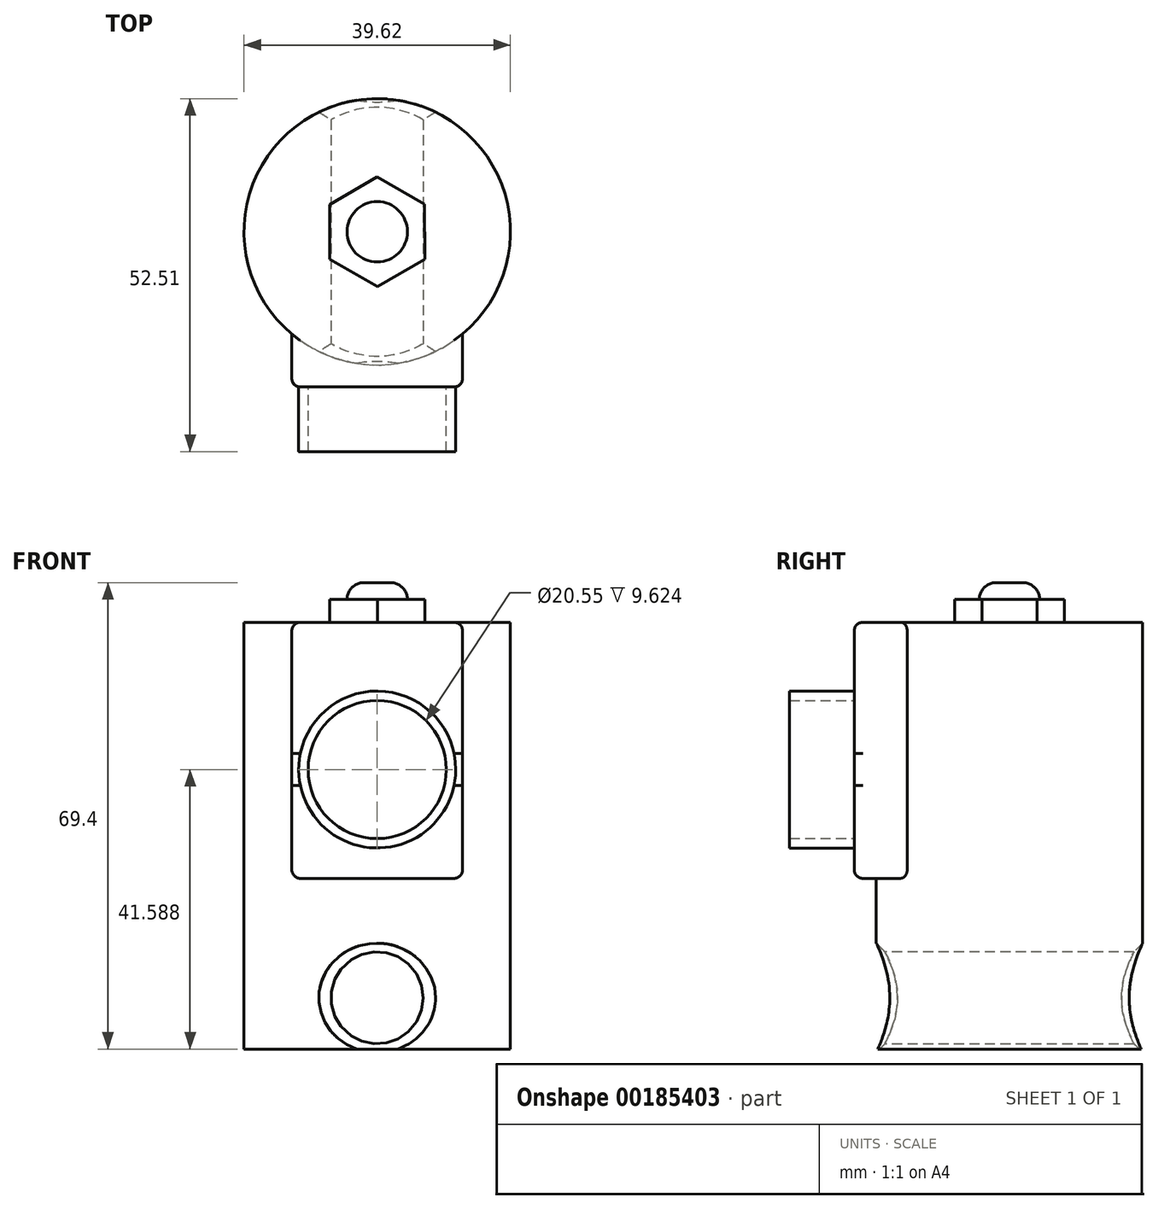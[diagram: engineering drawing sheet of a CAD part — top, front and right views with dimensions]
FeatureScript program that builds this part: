
annotation { "Feature Type Name" : "Feature", "Feature Type Description" : "" }
export const myFeature = defineFeature(function(context is Context, id is Id, definition is map)
    precondition{}
    {
        {
            var Q0;
            Q0=qCreatedBy(makeId("Top.planeOp"),FACE);
            var sketch = newSketch(context, id + "F0", { "sketchPlane" : qUnion([Q0])});
            skCircle(sketch, "E0", {"center": v(0, 0) * mm, "radius": 19.81 * mm});
            skLineSegment(sketch, "E1", {"start": v(0, 0) * mm, "end": v(0, -19.81) * mm});
            skSolve(sketch);
        }
        {
            var Q0;
            Q0 = qSketchRegion(id + "F0", true);
            extrude(context, id + "F1", {"entities" : qUnion([Q0]), "depth" : 63.5 * mm});
        }
        {
            var Q0;
            Q0=qCreatedBy(makeId("Right.planeOp"),FACE);
            var sketch = newSketch(context, id + "F2", { "sketchPlane" : qUnion([Q0])});
            skLineSegment(sketch, "E2", {"start": v(-19.81, 0) * mm, "end": v(-19.81, 70.78) * mm});
            skSolve(sketch);
        }
        {
            var Q0;
            Q0=sQuery(id+"F2.wireOp",EDGE,"E2");
            cPlane(context, id + "F3", {"entities" : qUnion([Q0]), "cplaneType" : CPlaneType.LINE_ANGLE, "offset" : 25.4 * mm, "angle" : 90 * degree, "width" : 152.4 * mm, "height" : 152.4 * mm});
        }
        {
            var Q0;
            Q0=qCreatedBy(id+"F3.planeOp",FACE);
            var sketch = newSketch(context, id + "F4", { "sketchPlane" : qUnion([Q0])});
            skLineSegment(sketch, "E3", {"start": v(0, 0) * mm, "end": v(0, 7.62) * mm});
            skCircle(sketch, "E4", {"center": v(0, 7.62) * mm, "radius": 6.86 * mm});
            skSolve(sketch);
        }
        {
            var Q0;
            Q0=makeQuery(id+"F4.imprint","IMPRINT",FACE,{"disambiguationData":[TD([[makeQuery(id+"F4.imprint","IMPRINT",EDGE,{"derivedFrom":sQuery(id+"F4.wireOp",EDGE,"E4")}),1.0]])]});
            extrude(context, id + "F5", {"entities" : qUnion([Q0]), "operationType" : NewBodyOperationType.REMOVE, "depth" : 50.8 * mm});
        }
        {
            var Q0;
            Q0=qCreatedBy(id+"F3.planeOp",FACE);
            var sketch = newSketch(context, id + "F6", { "sketchPlane" : qUnion([Q0])});
            skLineSegment(sketch, "E5", {"start": v(0, 63.5) * mm, "end": v(0, 44.45) * mm});
            skLineSegment(sketch, "E6.bottom", {"start": v(-12.7, 63.5) * mm, "end": v(12.7, 63.5) * mm});
            skLineSegment(sketch, "E6.top", {"start": v(-12.7, 25.4) * mm, "end": v(12.7, 25.4) * mm});
            skLineSegment(sketch, "E6.left", {"start": v(-12.7, 63.5) * mm, "end": v(-12.7, 25.4) * mm});
            skLineSegment(sketch, "E6.right", {"start": v(12.7, 63.5) * mm, "end": v(12.7, 25.4) * mm});
            skPoint(sketch, "E6.middle", {"position": v(0, 44.45) * mm});
            skSolve(sketch);
        }
        {
            var Q0;
            Q0=makeQuery(id+"F6.imprint","IMPRINT",FACE,{"disambiguationData":[TD([[makeQuery(id+"F6.imprint","IMPRINT",EDGE,{"derivedFrom":sQuery(id+"F6.wireOp",EDGE,"E6.top")}),1.0]])]});
            extrude(context, id + "F7", {"entities" : qUnion([Q0]), "operationType" : NewBodyOperationType.ADD, "depth" : 25.4 * mm, "hasSecondDirection" : true, "secondDirectionOppositeDirection" : true, "secondDirectionDepth" : 3.27 * mm});
        }
        {
            var Q0;
            Q0=makeQuery(id+"F7.opExtrude","CAP_FACE",FACE,{"disambiguationData":[OSD([sQuery(id+"F6.wireOp",EDGE,"E6.bottom"),sQuery(id+"F6.wireOp",EDGE,"E6.top"),sQuery(id+"F6.wireOp",EDGE,"E6.left"),sQuery(id+"F6.wireOp",EDGE,"E6.right")])],"isStart":true});
            var sketch = newSketch(context, id + "F8", { "sketchPlane" : qUnion([Q0])});
            skCircle(sketch, "E7", {"center": v(0, 41.59) * mm, "radius": 11.67 * mm});
            skCircle(sketch, "E8", {"center": v(0, 41.59) * mm, "radius": 10.27 * mm});
            skSolve(sketch);
        }
        {
            var Q0;
            Q0=makeQuery(id+"F8.imprint","IMPRINT",FACE,{"disambiguationData":[TD([[makeQuery(id+"F8.imprint","IMPRINT",EDGE,{"derivedFrom":sQuery(id+"F8.wireOp",EDGE,"E7")}),1.0]])]});
            extrude(context, id + "F9", {"entities" : qUnion([Q0]), "operationType" : NewBodyOperationType.ADD, "depth" : 9.62 * mm});
        }
        {
            var Q0;
            Q0=makeQuery(id+"F7.boolean.opBoolean","MERGE",FACE,{"derivedFrom":[makeQuery(id+"F1.opExtrude","CAP_FACE",FACE,{"disambiguationData":[OSD([sQuery(id+"F0.wireOp",EDGE,"E0")])],"isStart":false}),makeQuery(id+"F7.opExtrude","SWEPT_FACE",FACE,{"disambiguationData":[OSD([sQuery(id+"F6.wireOp",EDGE,"E6.bottom")])]})]});
            var sketch = newSketch(context, id + "F10", { "sketchPlane" : qUnion([Q0])});
            skCircle(sketch, "E9.cCircle", {"center": v(0, 0) * mm, "radius": 8.16 * mm, "construction": true});
            skLineSegment(sketch, "E9.0", {"start": v(7.05, 4.1) * mm, "end": v(7.09, -4.06) * mm});
            skLineSegment(sketch, "E9.1", {"start": v(7.09, -4.06) * mm, "end": v(0.03, -8.16) * mm});
            skLineSegment(sketch, "E9.2", {"start": v(0.03, -8.16) * mm, "end": v(-7.05, -4.1) * mm});
            skLineSegment(sketch, "E9.3", {"start": v(-7.05, -4.1) * mm, "end": v(-7.09, 4.06) * mm});
            skLineSegment(sketch, "E9.4", {"start": v(-7.09, 4.06) * mm, "end": v(-0.03, 8.16) * mm});
            skLineSegment(sketch, "E9.5", {"start": v(-0.03, 8.16) * mm, "end": v(7.05, 4.1) * mm});
            skSolve(sketch);
        }
        {
            var Q0;
            Q0=makeQuery(id+"F10.imprint","IMPRINT",FACE,{"disambiguationData":[TD([[makeQuery(id+"F10.imprint","IMPRINT",EDGE,{"derivedFrom":sQuery(id+"F10.wireOp",EDGE,"E9.0")}),-1.0]])]});
            extrude(context, id + "F11", {"entities" : qUnion([Q0]), "operationType" : NewBodyOperationType.ADD, "depth" : 3.38 * mm});
        }
        {
            var Q0;
            Q0=makeQuery(id+"F11.opExtrude","CAP_FACE",FACE,{"disambiguationData":[OSD([sQuery(id+"F10.wireOp",EDGE,"E9.0"),sQuery(id+"F10.wireOp",EDGE,"E9.1"),sQuery(id+"F10.wireOp",EDGE,"E9.2"),sQuery(id+"F10.wireOp",EDGE,"E9.3"),sQuery(id+"F10.wireOp",EDGE,"E9.4"),sQuery(id+"F10.wireOp",EDGE,"E9.5")])],"isStart":false});
            var sketch = newSketch(context, id + "F12", { "sketchPlane" : qUnion([Q0])});
            skCircle(sketch, "E10", {"center": v(0, 0) * mm, "radius": 4.5 * mm});
            skSolve(sketch);
        }
        {
            var Q0;
            Q0=makeQuery(id+"F12.imprint","IMPRINT",FACE,{"disambiguationData":[TD([[makeQuery(id+"F12.imprint","IMPRINT",EDGE,{"derivedFrom":sQuery(id+"F12.wireOp",EDGE,"E10")}),1.0]])]});
            extrude(context, id + "F13", {"entities" : qUnion([Q0]), "operationType" : NewBodyOperationType.ADD, "depth" : 2.53 * mm});
        }
        {
            var Q0;
            Q0=makeQuery(id+"F13.opExtrude","CAP_EDGE",EDGE,{"disambiguationData":[OSD([sQuery(id+"F12.wireOp",EDGE,"E10")])],"isStart":false});
            fillet(context, id + "F14", {"entities" : qUnion([Q0]), "radius" : 2.54 * mm, "tangentPropagation" : true, "allowEdgeOverflow" : false});
        }
        {
            var Q0;
            Q0=makeQuery(id+"F9.opExtrude","CAP_EDGE",EDGE,{"disambiguationData":[OSD([sQuery(id+"F8.wireOp",EDGE,"E7")])],"isStart":true});
            var Q1;
            Q1=makeQuery(id+"F7.opExtrude","CAP_EDGE",EDGE,{"disambiguationData":[OSD([sQuery(id+"F6.wireOp",EDGE,"E6.bottom")])],"isStart":true});
            var Q2;
            Q2=makeQuery(id+"F7.opExtrude","CAP_EDGE",EDGE,{"disambiguationData":[OSD([sQuery(id+"F6.wireOp",EDGE,"E6.top")])],"isStart":true});
            fillet(context, id + "F15", {"entities" : qUnion([Q0, Q1, Q2]), "radius" : 1.27 * mm, "tangentPropagation" : true, "allowEdgeOverflow" : false});
        }
        {
            var Q0;
            Q0=makeQuery(id+"F7.opExtrude","CAP_EDGE",EDGE,{"disambiguationData":[OSD([sQuery(id+"F6.wireOp",EDGE,"E6.left")])],"isStart":true});
            var Q1;
            Q1=makeQuery(id+"F7.opExtrude","CAP_EDGE",EDGE,{"disambiguationData":[OSD([sQuery(id+"F6.wireOp",EDGE,"E6.right")])],"isStart":true});
            fillet(context, id + "F16", {"entities" : qUnion([Q0, Q1]), "radius" : 1.27 * mm, "tangentPropagation" : true, "allowEdgeOverflow" : false});
        }
        {
            var Q0;
            Q0=makeQuery(id+"F5.boolean.opBoolean","INTERSECT",EDGE,{"derivedFrom":[makeQuery(id+"F1.opExtrude","SWEPT_FACE",FACE,{"disambiguationData":[OSD([sQuery(id+"F0.wireOp",EDGE,"E0")])]}),makeQuery(id+"F5.opExtrude","SWEPT_FACE",FACE,{"disambiguationData":[OSD([sQuery(id+"F4.wireOp",EDGE,"E4")])]})]});
            chamfer(context, id + "F17", {"entities" : qUnion([Q0]), "width" : 1.27 * mm, "tangentPropagation" : true});
        }
    });
